# Revit family: KKDC_TANA_kR207_3000K_1020mm
name_source: partatom
category: 조명 설비
units: mm (PartAtom-declared; Revit-internal decimal feet)

## family parameters
OmniClass 번호 = 23.80.70.00
OmniClass 제목 = Lighting
공유 = 아니오
광원 = 예
로드될 때 보이드를 사용하여 절단 = 아니오
룸 계산 점 = 아니오
부품 유형 = 배선함
원형 커넥터 치수 = 지름 사용
작업 기준면 기반 = 예
주석 방향 유지 = 아니오
항상 수직 = 예

## types (2) — shared parameters
Height = 18  [stored 0.0590551 ft]
Length = 1020  [stored 3.34646 ft]
Width = 25  [stored 0.082021 ft]
감광 램프 색상 온도 변화 = <없음>
경사도 = 157.00°
램프 = kR207
렌더링 시 발산 모양 표시 = 아니오
색상 필터 = 16777215
와티지 해설 = 16W/m
직사각형 길이에서 발산 = 13.5  [stored 0.0442913 ft]
직사각형 폭에서 발산 = 1010  [stored 3.31365 ft]
zero-valued in all types: 기본 높이

## per-type parameters (varying)
| type | 측광 웹 파일 |
| TANA kR207 2100K + 5000K Clear 1020mm | TANA Clear Cover R207(k-line).IES |
| TANA kR207 2100K + 5000K Diffused 1020mm | TANA Diffused Cover R207(k-line).IES |

note: [stored X ft] marks values corroborated as IEEE doubles in the binary element streams (Revit-internal decimal feet)
